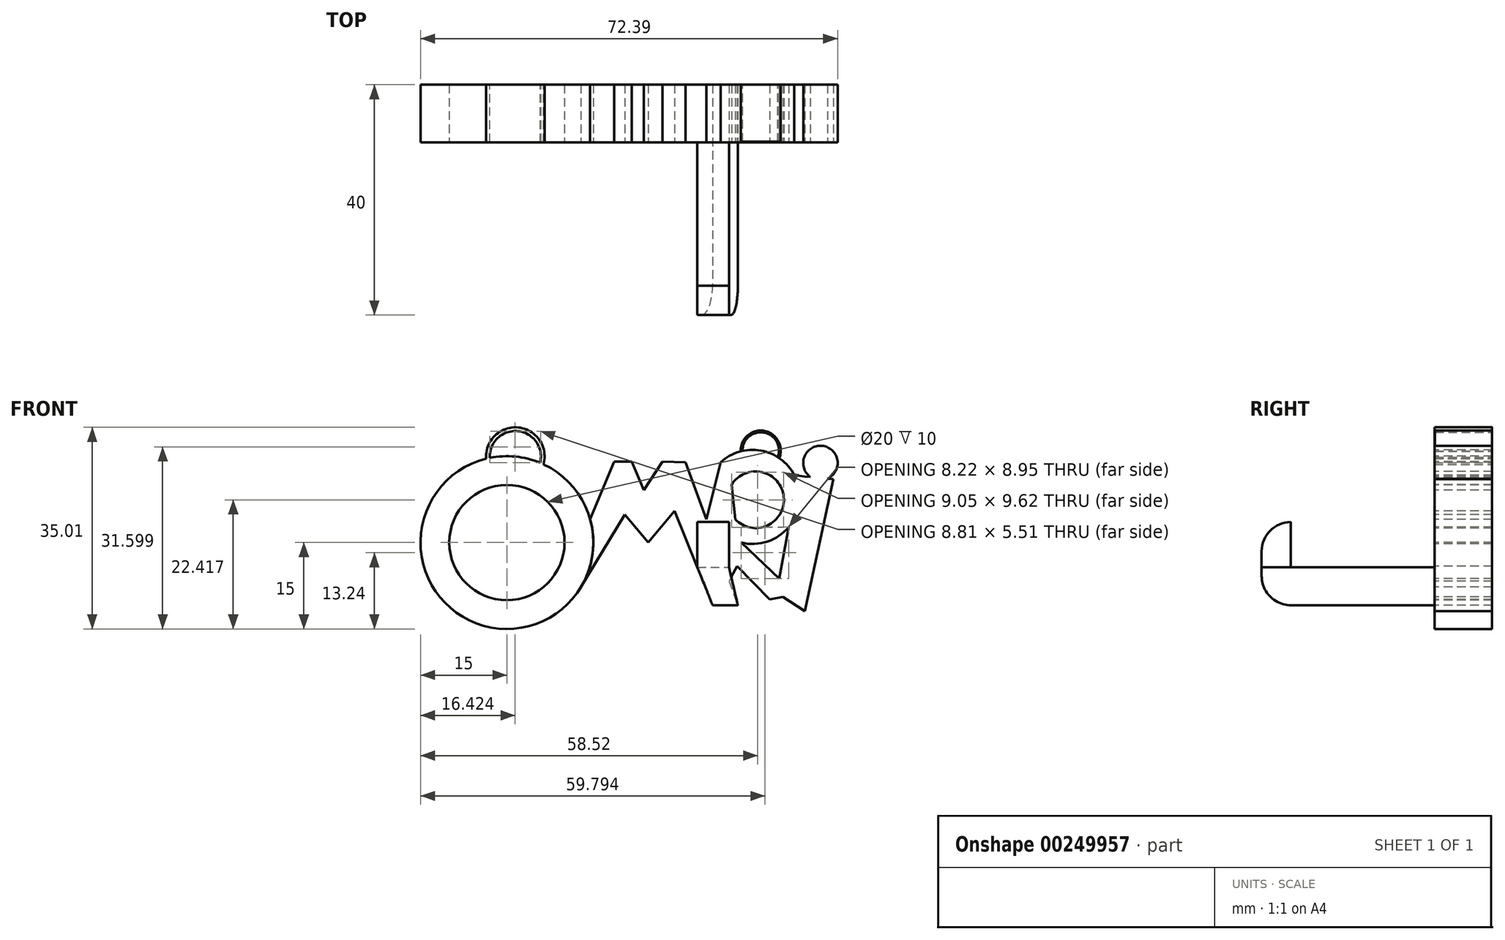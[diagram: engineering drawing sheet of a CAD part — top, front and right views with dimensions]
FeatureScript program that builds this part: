
annotation { "Feature Type Name" : "Feature", "Feature Type Description" : "" }
export const myFeature = defineFeature(function(context is Context, id is Id, definition is map)
    precondition{}
    {
        {
            var Q0;
            Q0=qCreatedBy(makeId("Front.planeOp"),FACE);
            var sketch = newSketch(context, id + "F0", { "sketchPlane" : qUnion([Q0])});
            skCircle(sketch, "E0", {"center": v(0, 0) * mm, "radius": 10 * mm});
            skCircle(sketch, "E1", {"center": v(0, 0) * mm, "radius": 15 * mm});
            skLineSegment(sketch, "E2", {"start": v(14.45, 4.04) * mm, "end": v(18.63, 14.1) * mm});
            skLineSegment(sketch, "E3", {"start": v(18.63, 14.1) * mm, "end": v(21.68, 14.1) * mm});
            skLineSegment(sketch, "E4", {"start": v(21.68, 14.1) * mm, "end": v(23.77, 9.13) * mm});
            skLineSegment(sketch, "E5", {"start": v(23.77, 9.13) * mm, "end": v(26.98, 14.1) * mm});
            skLineSegment(sketch, "E6", {"start": v(26.98, 14.1) * mm, "end": v(31.01, 13.96) * mm});
            skLineSegment(sketch, "E7", {"start": v(31.01, 13.96) * mm, "end": v(40.08, -10.89) * mm});
            skLineSegment(sketch, "E8", {"start": v(40.08, -10.89) * mm, "end": v(35.7, -10.89) * mm});
            skLineSegment(sketch, "E9", {"start": v(35.7, -10.89) * mm, "end": v(29.11, 5.51) * mm});
            skLineSegment(sketch, "E10", {"start": v(29.11, 5.51) * mm, "end": v(24.54, 0) * mm});
            skLineSegment(sketch, "E11", {"start": v(24.54, 0) * mm, "end": v(20.44, 4.84) * mm});
            skLineSegment(sketch, "E12", {"start": v(20.44, 4.84) * mm, "end": v(12.85, -7.75) * mm});
            skLineSegment(sketch, "E13", {"start": v(34.63, 4.04) * mm, "end": v(37.1, 13.96) * mm});
            skArc(sketch, "E14", {"start": v(40.68, 0) * mm, "mid": v(50.54, 9.96) * mm, "end": v(37.1, 13.96) * mm});
            skArc(sketch, "E15", {"start": v(39.6, 4.04) * mm, "mid": v(48.04, 7.93) * mm, "end": v(39, 10.07) * mm});
            skLineSegment(sketch, "E16", {"start": v(40.68, 0) * mm, "end": v(50.12, -8.95) * mm});
            skLineSegment(sketch, "E17", {"start": v(50.12, -8.95) * mm, "end": v(45.6, -9.89) * mm});
            skLineSegment(sketch, "E18", {"start": v(45.6, -9.89) * mm, "end": v(39.94, -4.1) * mm});
            skLineSegment(sketch, "E19", {"start": v(39.94, -4.1) * mm, "end": v(38.54, -6.67) * mm});
            skLineSegment(sketch, "E20", {"start": v(39, 10.07) * mm, "end": v(39.6, 4.04) * mm});
            skLineSegment(sketch, "E21", {"start": v(51.69, 11.48) * mm, "end": v(56.62, 11) * mm});
            skLineSegment(sketch, "E22", {"start": v(56.62, 11) * mm, "end": v(51.69, -11.88) * mm});
            skLineSegment(sketch, "E23", {"start": v(51.69, -11.88) * mm, "end": v(47.86, -9.42) * mm});
            skArc(sketch, "E24", {"start": v(55.66, 11.1) * mm, "mid": v(54.69, 16.8) * mm, "end": v(52.66, 11.39) * mm});
            skArc(sketch, "E25", {"start": v(12.85, -7.75) * mm, "mid": v(14.86, -2.02) * mm, "end": v(14.45, 4.04) * mm});
            skLineSegment(sketch, "E26", {"start": v(47.26, -6.23) * mm, "end": v(48.9, 2.71) * mm});
            skLineSegment(sketch, "E27", {"start": v(49.87, 11.7) * mm, "end": v(51.69, 11.48) * mm});
            skArc(sketch, "E28", {"start": v(48.9, 2.71) * mm, "mid": v(50.75, 7.06) * mm, "end": v(49.87, 11.7) * mm});
            skSolve(sketch);
        }
        {
            var Q0;
            Q0=makeQuery(id+"F0.imprint","IMPRINT",FACE,{"disambiguationData":[TD([[makeQuery(id+"F0.imprint","IMPRINT",EDGE,{"derivedFrom":sQuery(id+"F0.wireOp",EDGE,"E0")}),-1.0]])]});
            extrude(context, id + "F1", {"entities" : qUnion([Q0]), "oppositeDirection" : true, "depth" : 10 * mm});
        }
        {
            var Q0;
            {var subQ7=sQuery(id+"F0.wireOp",EDGE,"E2");Q0=makeQuery(id+"F0.imprint","IMPRINT",FACE,{"disambiguationData":[TD([[makeQuery(id+"F0.imprint","IMPRINT",EDGE,{"derivedFrom":subQ7}),-1.0]])]});}
            extrude(context, id + "F2", {"entities" : qUnion([Q0]), "oppositeDirection" : true, "depth" : 10 * mm});
        }
        {
            var Q0;
            {var subQ10=sQuery(id+"F0.wireOp",EDGE,"E13");Q0=makeQuery(id+"F0.imprint","IMPRINT",FACE,{"disambiguationData":[TD([[makeQuery(id+"F0.imprint","IMPRINT",EDGE,{"derivedFrom":subQ10}),-1.0]])]});}
            extrude(context, id + "F3", {"entities" : qUnion([Q0]), "operationType" : NewBodyOperationType.ADD, "oppositeDirection" : true, "depth" : 10 * mm});
        }
        {
            var Q0;
            {var subQ10=sQuery(id+"F0.wireOp",EDGE,"E22");Q0=makeQuery(id+"F0.imprint","IMPRINT",FACE,{"disambiguationData":[TD([[makeQuery(id+"F0.imprint","IMPRINT",EDGE,{"derivedFrom":subQ10}),-1.0]])]});}
            var Q1;
            {var subQ0=sQuery(id+"F0.wireOp",EDGE,"E24");Q1=makeQuery(id+"F0.imprint","IMPRINT",FACE,{"disambiguationData":[TD([[makeQuery(id+"F0.imprint","IMPRINT",EDGE,{"derivedFrom":subQ0}),1.0]])]});}
            extrude(context, id + "F4", {"entities" : qUnion([Q0, Q1]), "operationType" : NewBodyOperationType.ADD, "oppositeDirection" : true, "depth" : 10 * mm});
        }
        {
            var Q0;
            {var subQ0=sQuery(id+"F0.wireOp",EDGE,"E17");var subQ1=sQuery(id+"F0.wireOp",EDGE,"E16");var subQ2=sQuery(id+"F0.wireOp",EDGE,"E7");Q0=makeQuery(id+"F4.boolean.opBoolean","MERGE",FACE,{"derivedFrom":[makeQuery(id+"F3.boolean.opBoolean","MERGE",FACE,{"derivedFrom":[makeQuery(id+"F2.opExtrude","CAP_FACE",FACE,{"disambiguationData":[OSD([sQuery(id+"F0.wireOp",EDGE,"E1"),sQuery(id+"F0.wireOp",EDGE,"E2"),sQuery(id+"F0.wireOp",EDGE,"E3"),sQuery(id+"F0.wireOp",EDGE,"E4"),sQuery(id+"F0.wireOp",EDGE,"E5"),sQuery(id+"F0.wireOp",EDGE,"E6"),subQ2,sQuery(id+"F0.wireOp",EDGE,"E8"),sQuery(id+"F0.wireOp",EDGE,"E9"),sQuery(id+"F0.wireOp",EDGE,"E10"),sQuery(id+"F0.wireOp",EDGE,"E11"),sQuery(id+"F0.wireOp",EDGE,"E12")])],"isStart":true}),makeQuery(id+"F3.opExtrude","CAP_FACE",FACE,{"disambiguationData":[OSD([subQ2,sQuery(id+"F0.wireOp",EDGE,"E13"),sQuery(id+"F0.wireOp",EDGE,"E14"),sQuery(id+"F0.wireOp",EDGE,"E15"),subQ1,subQ0,sQuery(id+"F0.wireOp",EDGE,"E18"),sQuery(id+"F0.wireOp",EDGE,"E19"),sQuery(id+"F0.wireOp",EDGE,"E20")])],"isStart":true})]}),makeQuery(id+"F4.opExtrude","CAP_FACE",FACE,{"disambiguationData":[OSD([subQ1,subQ0,sQuery(id+"F0.wireOp",EDGE,"E21"),sQuery(id+"F0.wireOp",EDGE,"E22"),sQuery(id+"F0.wireOp",EDGE,"E23"),sQuery(id+"F0.wireOp",EDGE,"E24"),sQuery(id+"F0.wireOp",EDGE,"E26"),sQuery(id+"F0.wireOp",EDGE,"E27"),sQuery(id+"F0.wireOp",EDGE,"E28")])],"isStart":true})]});}
            var sketch = newSketch(context, id + "F5", { "sketchPlane" : qUnion([Q0])});
            skLineSegment(sketch, "E29", {"start": v(35.7, -10.89) * mm, "end": v(33.05, -4.3) * mm});
            skLineSegment(sketch, "E30", {"start": v(33.05, -4.3) * mm, "end": v(38.54, -4.3) * mm});
            skLineSegment(sketch, "E31", {"start": v(38.54, -4.3) * mm, "end": v(40.08, -10.89) * mm});
            skLineSegment(sketch, "E32", {"start": v(40.08, -10.89) * mm, "end": v(35.7, -10.89) * mm});
            skSolve(sketch);
        }
        {
            var Q0;
            Q0 = qSketchRegion(id + "F5", true);
            extrude(context, id + "F6", {"entities" : qUnion([Q0]), "operationType" : NewBodyOperationType.ADD, "depth" : 30 * mm});
        }
        {
            var Q0;
            Q0=makeQuery(id+"F6.opExtrude","SWEPT_FACE",FACE,{"disambiguationData":[OSD([sQuery(id+"F5.wireOp",EDGE,"E30")])]});
            var sketch = newSketch(context, id + "F7", { "sketchPlane" : qUnion([Q0])});
            skLineSegment(sketch, "E33.bottom", {"start": v(38.54, -24.94) * mm, "end": v(33.05, -24.94) * mm});
            skLineSegment(sketch, "E33.top", {"start": v(38.54, -30) * mm, "end": v(33.05, -30) * mm});
            skLineSegment(sketch, "E33.left", {"start": v(38.54, -24.94) * mm, "end": v(38.54, -30) * mm});
            skLineSegment(sketch, "E33.right", {"start": v(33.05, -24.94) * mm, "end": v(33.05, -30) * mm});
            skSolve(sketch);
        }
        {
            var Q0;
            Q0=makeQuery(id+"F7.imprint","IMPRINT",FACE,{"disambiguationData":[TD([[makeQuery(id+"F7.imprint","IMPRINT",EDGE,{"derivedFrom":sQuery(id+"F7.wireOp",EDGE,"E33.bottom")}),1.0]])]});
            extrude(context, id + "F8", {"entities" : qUnion([Q0]), "operationType" : NewBodyOperationType.ADD, "depth" : 7.87 * mm});
        }
        {
            var Q0;
            Q0=makeQuery(id+"F7N6K52G5EQYWSe_1.opExtrude","CAP_EDGE",EDGE,{"disambiguationData":[OSD([sQuery(id+"F3pw4Ykfb46Yntu_1.wireOp",EDGE,"bZw9rTlc-MOsV-1PP6-xSxm-7nMMBdoc1J3J.bottom")])],"isStart":false});
            var Q1;
            Q1=makeQuery(id+"F8.opExtrude","CAP_EDGE",EDGE,{"disambiguationData":[OSD([sQuery(id+"F7.wireOp",EDGE,"E33.top")])],"isStart":false});
            var Q2;
            Q2=makeQuery(id+"F6.opExtrude","CAP_EDGE",EDGE,{"disambiguationData":[OSD([sQuery(id+"F5.wireOp",EDGE,"E32")])],"isStart":false});
            fillet(context, id + "F9", {"entities" : qUnion([Q0, Q1, Q2]), "radius" : 5.08 * mm, "tangentPropagation" : true, "allowEdgeOverflow" : false});
        }
        {
            var Q0;
            Q0=makeQuery(id+"F1.opExtrude","CAP_FACE",FACE,{"disambiguationData":[OSD([sQuery(id+"F0.wireOp",EDGE,"E0"),sQuery(id+"F0.wireOp",EDGE,"E1")])],"isStart":false});
            var sketch = newSketch(context, id + "F10", { "sketchPlane" : qUnion([Q0])});
            skCircle(sketch, "E34", {"center": v(-1.46, 14.93) * mm, "radius": 5.08 * mm});
            skCircle(sketch, "E35", {"center": v(-1.46, 14.93) * mm, "radius": 4.45 * mm});
            skSolve(sketch);
        }
        {
            var Q0;
            {var subQ0=sQuery(id+"F10.wireOp",EDGE,"E34");var subQ1=makeQuery(id+"F1.opExtrude","CAP_EDGE",EDGE,{"disambiguationData":[OSD([sQuery(id+"F0.wireOp",EDGE,"E1")])],"isStart":false});var subQ2=makeQuery(id+"F10.imprint","INTERSECT",VERTEX,{"disambiguationData":[OD(0.0)],"derivedFrom":[subQ1,subQ0]});Q0=makeQuery(id+"F10.imprint","IMPRINT",FACE,{"disambiguationData":[TD([[makeQuery(id+"F10.imprint","IMPRINT",EDGE,{"disambiguationData":[TD([[subQ2,-1.0]])],"derivedFrom":subQ0}),1.0]])]});}
            extrude(context, id + "F11", {"entities" : qUnion([Q0]), "operationType" : NewBodyOperationType.ADD, "oppositeDirection" : true, "depth" : 1 * mm});
        }
        {
            var Q0;
            {var subQ0=sQuery(id+"F0.wireOp",EDGE,"E17");var subQ1=sQuery(id+"F0.wireOp",EDGE,"E16");var subQ2=sQuery(id+"F0.wireOp",EDGE,"E7");Q0=makeQuery(id+"F4.boolean.opBoolean","MERGE",FACE,{"derivedFrom":[makeQuery(id+"F3.boolean.opBoolean","MERGE",FACE,{"derivedFrom":[makeQuery(id+"F2.opExtrude","CAP_FACE",FACE,{"disambiguationData":[OSD([sQuery(id+"F0.wireOp",EDGE,"E1"),sQuery(id+"F0.wireOp",EDGE,"E2"),sQuery(id+"F0.wireOp",EDGE,"E3"),sQuery(id+"F0.wireOp",EDGE,"E4"),sQuery(id+"F0.wireOp",EDGE,"E5"),sQuery(id+"F0.wireOp",EDGE,"E6"),subQ2,sQuery(id+"F0.wireOp",EDGE,"E8"),sQuery(id+"F0.wireOp",EDGE,"E9"),sQuery(id+"F0.wireOp",EDGE,"E10"),sQuery(id+"F0.wireOp",EDGE,"E11"),sQuery(id+"F0.wireOp",EDGE,"E12")])],"isStart":false}),makeQuery(id+"F3.opExtrude","CAP_FACE",FACE,{"disambiguationData":[OSD([subQ2,sQuery(id+"F0.wireOp",EDGE,"E13"),sQuery(id+"F0.wireOp",EDGE,"E14"),sQuery(id+"F0.wireOp",EDGE,"E15"),subQ1,subQ0,sQuery(id+"F0.wireOp",EDGE,"E18"),sQuery(id+"F0.wireOp",EDGE,"E19"),sQuery(id+"F0.wireOp",EDGE,"E20")])],"isStart":false})]}),makeQuery(id+"F4.opExtrude","CAP_FACE",FACE,{"disambiguationData":[OSD([subQ1,subQ0,sQuery(id+"F0.wireOp",EDGE,"E21"),sQuery(id+"F0.wireOp",EDGE,"E22"),sQuery(id+"F0.wireOp",EDGE,"E23"),sQuery(id+"F0.wireOp",EDGE,"E24"),sQuery(id+"F0.wireOp",EDGE,"E26"),sQuery(id+"F0.wireOp",EDGE,"E27"),sQuery(id+"F0.wireOp",EDGE,"E28")])],"isStart":false})]});}
            var sketch = newSketch(context, id + "F12", { "sketchPlane" : qUnion([Q0])});
            skCircle(sketch, "E36", {"center": v(-44.05, 15.98) * mm, "radius": 3.47 * mm});
            skCircle(sketch, "E37", {"center": v(-44.05, 15.98) * mm, "radius": 3.18 * mm});
            skSolve(sketch);
        }
        {
            var Q0;
            {var subQ0=sQuery(id+"F12.wireOp",EDGE,"E36");var subQ3=sQuery(id+"F0.wireOp",EDGE,"E14");var subQ4=sQuery(id+"F0.wireOp",EDGE,"E13");var subQ7=makeQuery(id+"F4.boolean.opBoolean","SPLIT",EDGE,{"disambiguationData":[TD([makeQuery(id+"F3.opExtrude","SWEPT_FACE",FACE,{"disambiguationData":[OSD([subQ4])]})])],"derivedFrom":makeQuery(id+"F3.opExtrude","CAP_EDGE",EDGE,{"disambiguationData":[OSD([subQ3])],"isStart":false})});var subQ8=makeQuery(id+"F12.imprint","INTERSECT",VERTEX,{"disambiguationData":[OD(0.0)],"derivedFrom":[subQ7,subQ0]});Q0=makeQuery(id+"F12.imprint","IMPRINT",FACE,{"disambiguationData":[TD([[makeQuery(id+"F12.imprint","IMPRINT",EDGE,{"disambiguationData":[TD([[subQ8,-1.0]])],"derivedFrom":subQ0}),1.0]])]});}
            extrude(context, id + "F13", {"entities" : qUnion([Q0]), "oppositeDirection" : true, "depth" : 9.9 * mm});
        }
        {
            var Q0;
            {var subQ0=sQuery(id+"F10.wireOp",EDGE,"E34");var subQ1=makeQuery(id+"F1.opExtrude","CAP_EDGE",EDGE,{"disambiguationData":[OSD([sQuery(id+"F0.wireOp",EDGE,"E1")])],"isStart":false});var subQ2=makeQuery(id+"F10.imprint","INTERSECT",VERTEX,{"disambiguationData":[OD(0.0)],"derivedFrom":[subQ1,subQ0]});Q0=makeQuery(id+"F10.imprint","IMPRINT",FACE,{"disambiguationData":[TD([[makeQuery(id+"F10.imprint","IMPRINT",EDGE,{"disambiguationData":[TD([[subQ2,1.0]])],"derivedFrom":subQ0}),1.0]])]});}
            extrude(context, id + "F14", {"entities" : qUnion([Q0]), "operationType" : NewBodyOperationType.ADD, "oppositeDirection" : true, "depth" : 10 * mm});
        }
    });
